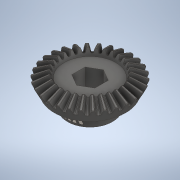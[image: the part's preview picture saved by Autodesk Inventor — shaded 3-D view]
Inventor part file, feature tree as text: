
AUTODESK INVENTOR PART (.ipt)
format: ipt  version: 2020 (Build 240168000, 168)  size: 1,945,088 bytes
history: native  units: in
note: dims shown in document units (in); Inventor stores cm internally (conversion verified against a paired STEP export)
features: extrude x1, sketch x1, imported_body x1
ambient origin geometry x8: Origin, YZ Plane, XZ Plane, XY Plane, X Axis, Y Axis, Z Axis, Center Point
bodies: Solid1 (feature_tree)
feature tree (3):
  extrude  "Extrusion2"  TaperAngle=0.0deg  [1 undecoded]
  sketch  "Sketch2"  dims[d3=0.5in d4=0.0in d5=0.0in]
  imported_body  "Base1"
note: 1 required parameter value undecoded (feature->parameter linkage not recoverable at this tier; creation-order binding heuristic only, values carry confidence <= 0.55)
